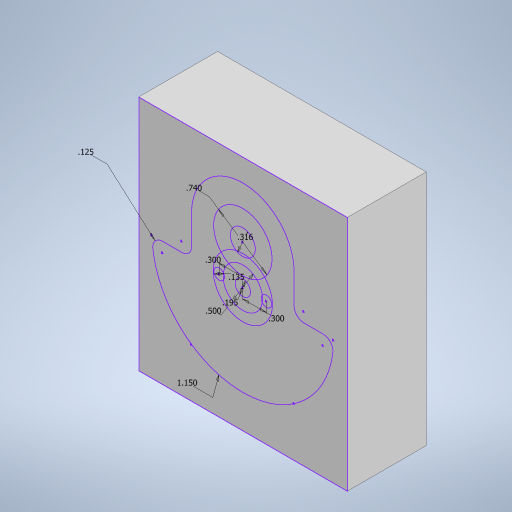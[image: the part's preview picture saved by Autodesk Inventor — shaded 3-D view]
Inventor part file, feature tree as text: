
AUTODESK INVENTOR PART (.ipt)
format: ipt  version: 2023 (Build 270158000, 158)  size: 522,752 bytes
history: native  units: in
note: dims shown in document units (in); Inventor stores cm internally (conversion verified against a paired STEP export)
features: extrude x10, fillet x2, draft x2, sketch x1
ambient origin geometry x8: Origin, YZ Plane, XZ Plane, XY Plane, X Axis, Y Axis, Z Axis, Center Point
bodies: Body1 (feature_tree)
feature tree (15):
  sketch  "Sketch1"  dims[d3=0.866in d15=0.75in d20=0.316in d37=0.75in d44=0.125in d57=0.74in d58=0.75in d59=0.0in d60=0.32in d61=0.0in d62=1.5in d63=0.0in d68=0.125in d70=0.135in d71=0.0206in d72=0.0412in d73=1.15in d76=0.3in d77=0.3in d78=1.0in d79=0.0in d80=1.0in d81=0.0in d84=0.5in d85=0.195in d86=0.5in d87=0.0in d88=0.5in d89=0.0in d90=0.5in d91=0.0in d92=0.005in d93=1.0in d94=0.0in d95=2.9375in d96=0.0in]
  extrude  "Extrusion9"  Depth=1.0in
  extrude  "Extrusion10"  Depth=1.0in
  extrude  "Extrusion11"  Depth=1.0in
  fillet  "Fillet2"  Radius=0.74in
  draft  "FaceDraft1"
  draft  "FaceDraft2"
  extrude  "Extrusion14"  Depth=1.0in TaperAngle=0.0deg
  extrude  "Extrusion15"  Depth=1.0in TaperAngle=0.0deg
  extrude  "Extrusion17"  Depth=1.0in TaperAngle=0.0deg
  extrude  "Extrusion18"  Depth=1.0in
  extrude  "Extrusion19"  Depth=1.0in
  fillet  "Fillet3"  Radius=0.0206in
  extrude  "Extrusion20"  Depth=1.0in
  extrude  "Extrusion21"  Depth=1.0in
